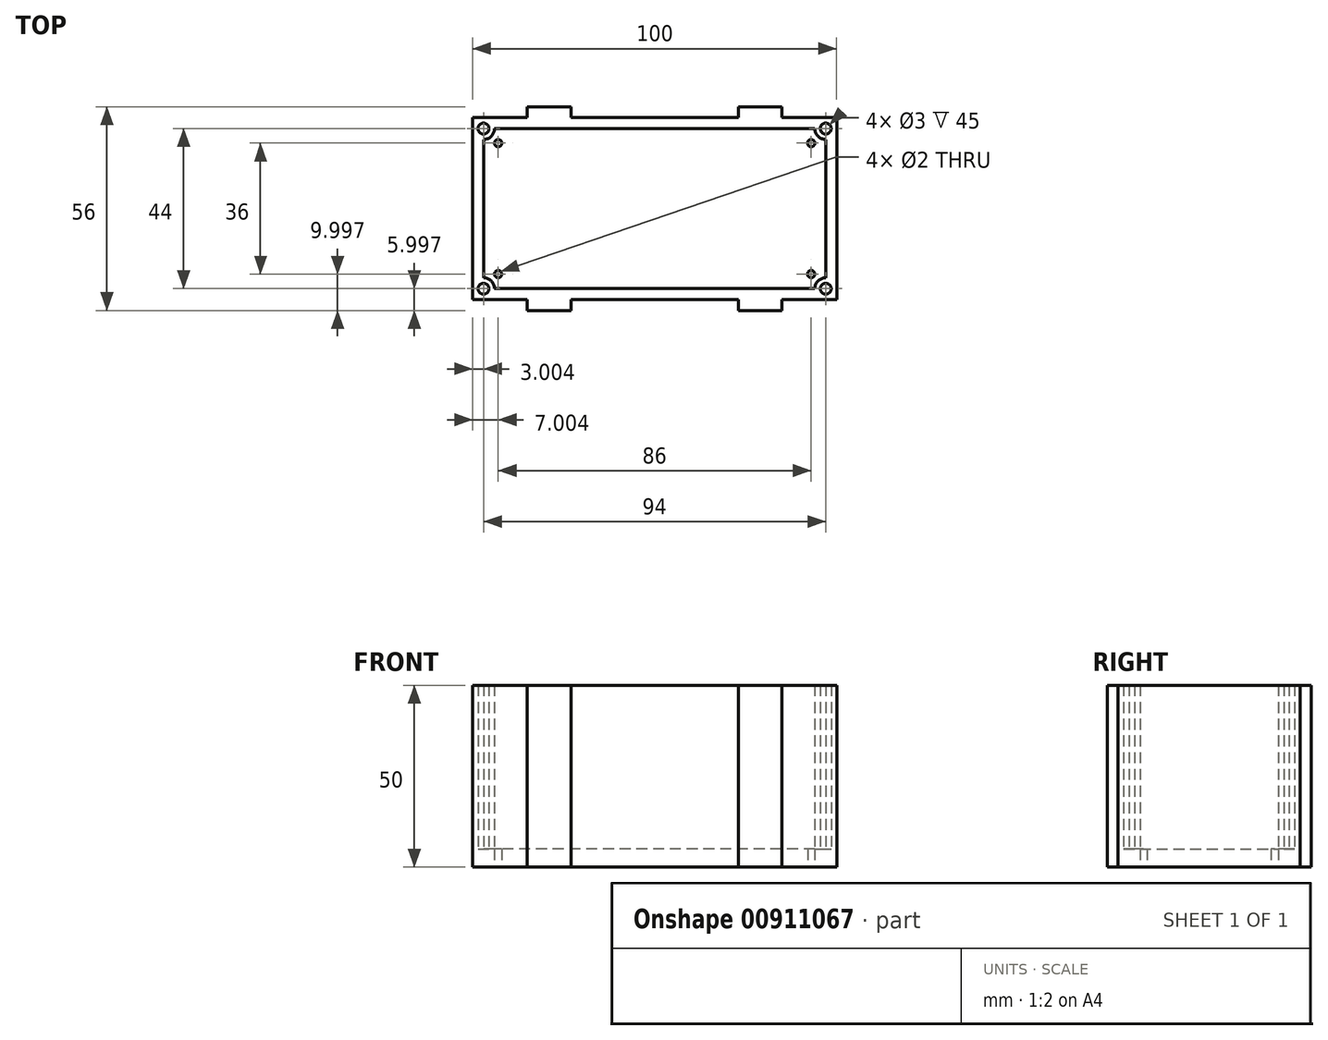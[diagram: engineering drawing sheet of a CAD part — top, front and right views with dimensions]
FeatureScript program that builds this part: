
annotation { "Feature Type Name" : "Feature", "Feature Type Description" : "" }
export const myFeature = defineFeature(function(context is Context, id is Id, definition is map)
    precondition{}
    {
        {
            var Q0;
            Q0=qCreatedBy(makeId("Top.planeOp"),FACE);
            var sketch = newSketch(context, id + "F0", { "sketchPlane" : qUnion([Q0])});
            skLineSegment(sketch, "E0.bottom", {"start": v(-49.27, 37.86) * mm, "end": v(50.73, 37.86) * mm});
            skLineSegment(sketch, "E0.top", {"start": v(-49.27, -12.14) * mm, "end": v(50.73, -12.14) * mm});
            skLineSegment(sketch, "E0.left", {"start": v(-49.27, 37.86) * mm, "end": v(-49.27, -12.14) * mm});
            skLineSegment(sketch, "E0.right", {"start": v(50.73, 37.86) * mm, "end": v(50.73, -12.14) * mm});
            skSolve(sketch);
        }
        {
            var Q0;
            Q0 = qSketchRegion(id + "F0", true);
            var Q1;
            Q1 = qSketchRegion(id + "F2", true);
            extrude(context, id + "F1", {"entities" : qUnion([Q0, Q1]), "depth" : 5 * mm, "offsetDistance" : 25 * mm});
        }
        {
            var Q0;
            Q0=makeQuery(id+"F1.opExtrude","CAP_FACE",FACE,{"disambiguationData":[OSD([sQuery(id+"F0.wireOp",EDGE,"E0.bottom"),sQuery(id+"F0.wireOp",EDGE,"E0.top"),sQuery(id+"F0.wireOp",EDGE,"E0.left"),sQuery(id+"F0.wireOp",EDGE,"E0.right")])],"isStart":false});
            var sketch = newSketch(context, id + "F2", { "sketchPlane" : qUnion([Q0])});
            skLineSegment(sketch, "E1.0", {"start": v(-46.27, 31.86) * mm, "end": v(-46.27, -6.14) * mm});
            skLineSegment(sketch, "E1.1", {"start": v(44.73, 34.86) * mm, "end": v(-43.27, 34.86) * mm});
            skLineSegment(sketch, "E1.2", {"start": v(47.73, -6.14) * mm, "end": v(47.73, 31.86) * mm});
            skLineSegment(sketch, "E1.3", {"start": v(-43.27, -9.14) * mm, "end": v(44.73, -9.14) * mm});
            skArc(sketch, "E2", {"start": v(-46.27, 31.86) * mm, "mid": v(-44.14, 32.74) * mm, "end": v(-43.27, 34.86) * mm});
            skArc(sketch, "E3", {"start": v(44.73, 34.86) * mm, "mid": v(45.61, 32.74) * mm, "end": v(47.73, 31.86) * mm});
            skArc(sketch, "E4", {"start": v(47.73, -6.14) * mm, "mid": v(45.61, -7.02) * mm, "end": v(44.73, -9.14) * mm});
            skArc(sketch, "E5", {"start": v(-43.27, -9.14) * mm, "mid": v(-44.14, -7.02) * mm, "end": v(-46.27, -6.14) * mm});
            skSolve(sketch);
        }
        {
            var Q0;
            Q0=makeQuery(id+"F2.imprint","IMPRINT",FACE,{"disambiguationData":[TD([[makeQuery(id+"F2.imprint","IMPRINT",EDGE,{"derivedFrom":sQuery(id+"F2.wireOp",EDGE,"E1.0")}),-1.0]])]});
            extrude(context, id + "F3", {"entities" : qUnion([Q0]), "operationType" : NewBodyOperationType.ADD, "depth" : 45 * mm, "offsetDistance" : 25 * mm});
        }
        {
            var Q0;
            {var subQ0=sQuery(id+"F0.wireOp",EDGE,"E0.top");Q0=makeQuery(id+"F3.boolean.opBoolean","MERGE",FACE,{"derivedFrom":[makeQuery(id+"F1.opExtrude","SWEPT_FACE",FACE,{"disambiguationData":[OSD([subQ0])]}),makeQuery(id+"F3.opExtrude","SWEPT_FACE",FACE,{"disambiguationData":[OSD([subQ0])]})]});}
            var sketch = newSketch(context, id + "F4", { "sketchPlane" : qUnion([Q0])});
            skLineSegment(sketch, "E6.bottom", {"start": v(-34.27, 0) * mm, "end": v(-22.27, 0) * mm});
            skLineSegment(sketch, "E6.top", {"start": v(-34.27, 50) * mm, "end": v(-22.27, 50) * mm});
            skLineSegment(sketch, "E6.left", {"start": v(-34.27, 0) * mm, "end": v(-34.27, 50) * mm});
            skLineSegment(sketch, "E6.right", {"start": v(-22.27, 0) * mm, "end": v(-22.27, 50) * mm});
            skLineSegment(sketch, "E7.bottom", {"start": v(23.73, 0) * mm, "end": v(35.73, 0) * mm});
            skLineSegment(sketch, "E7.top", {"start": v(23.73, 50) * mm, "end": v(35.73, 50) * mm});
            skLineSegment(sketch, "E7.left", {"start": v(23.73, 0) * mm, "end": v(23.73, 50) * mm});
            skLineSegment(sketch, "E7.right", {"start": v(35.73, 0) * mm, "end": v(35.73, 50) * mm});
            skSolve(sketch);
        }
        {
            var Q0;
            Q0=makeQuery(id+"F4.imprint","IMPRINT",FACE,{"disambiguationData":[TD([[makeQuery(id+"F4.imprint","IMPRINT",EDGE,{"derivedFrom":sQuery(id+"F4.wireOp",EDGE,"E6.bottom")}),1.0]])]});
            var Q1;
            Q1=makeQuery(id+"F4.imprint","IMPRINT",FACE,{"disambiguationData":[TD([[makeQuery(id+"F4.imprint","IMPRINT",EDGE,{"derivedFrom":sQuery(id+"F4.wireOp",EDGE,"E7.bottom")}),1.0]])]});
            extrude(context, id + "F5", {"entities" : qUnion([Q0, Q1]), "operationType" : NewBodyOperationType.ADD, "depth" : 3 * mm, "offsetDistance" : 25 * mm});
        }
        {
            var Q0;
            {var subQ0=sQuery(id+"F0.wireOp",EDGE,"E0.bottom");Q0=makeQuery(id+"F3.boolean.opBoolean","MERGE",FACE,{"derivedFrom":[makeQuery(id+"F1.opExtrude","SWEPT_FACE",FACE,{"disambiguationData":[OSD([subQ0])]}),makeQuery(id+"F3.opExtrude","SWEPT_FACE",FACE,{"disambiguationData":[OSD([subQ0])]})]});}
            var sketch = newSketch(context, id + "F6", { "sketchPlane" : qUnion([Q0])});
            skLineSegment(sketch, "E8.bottom", {"start": v(-35.73, 50) * mm, "end": v(-23.73, 50) * mm});
            skLineSegment(sketch, "E8.top", {"start": v(-35.73, 0) * mm, "end": v(-23.73, 0) * mm});
            skLineSegment(sketch, "E8.left", {"start": v(-35.73, 50) * mm, "end": v(-35.73, 0) * mm});
            skLineSegment(sketch, "E8.right", {"start": v(-23.73, 50) * mm, "end": v(-23.73, 0) * mm});
            skLineSegment(sketch, "E9.bottom", {"start": v(22.27, 50) * mm, "end": v(34.27, 50) * mm});
            skLineSegment(sketch, "E9.top", {"start": v(22.27, 0) * mm, "end": v(34.27, 0) * mm});
            skLineSegment(sketch, "E9.left", {"start": v(22.27, 50) * mm, "end": v(22.27, 0) * mm});
            skLineSegment(sketch, "E9.right", {"start": v(34.27, 50) * mm, "end": v(34.27, 0) * mm});
            skSolve(sketch);
        }
        {
            var Q0;
            Q0=makeQuery(id+"F6.imprint","IMPRINT",FACE,{"disambiguationData":[TD([[makeQuery(id+"F6.imprint","IMPRINT",EDGE,{"derivedFrom":sQuery(id+"F6.wireOp",EDGE,"E8.bottom")}),1.0]])]});
            var Q1;
            Q1=makeQuery(id+"F6.imprint","IMPRINT",FACE,{"disambiguationData":[TD([[makeQuery(id+"F6.imprint","IMPRINT",EDGE,{"derivedFrom":sQuery(id+"F6.wireOp",EDGE,"E9.bottom")}),1.0]])]});
            extrude(context, id + "F7", {"entities" : qUnion([Q0, Q1]), "operationType" : NewBodyOperationType.ADD, "depth" : 3 * mm, "offsetDistance" : 25 * mm});
        }
        {
            var Q0;
            Q0=sQuery(id+"F2.wireOp",VERTEX,"E2.center");
            var Q1;
            Q1=sQuery(id+"F2.wireOp",VERTEX,"E5.center");
            var Q2;
            Q2=sQuery(id+"F2.wireOp",VERTEX,"E3.center");
            var Q3;
            Q3=sQuery(id+"F2.wireOp",VERTEX,"E4.center");
            var Q4;
            Q4=makeQuery(id+"F1.opExtrude","SWEPT_BODY",BODY,{"disambiguationData":[OSD([sQuery(id+"F0.wireOp",EDGE,"E0.bottom"),sQuery(id+"F0.wireOp",EDGE,"E0.top"),sQuery(id+"F0.wireOp",EDGE,"E0.left"),sQuery(id+"F0.wireOp",EDGE,"E0.right")])]});
            hole(context, id + "F8", {"style" : HoleStyle.SIMPLE, "endStyle" : HoleEndStyle.BLIND, "oppositeDirection" : true, "holeDiameter" : 3 * mm, "majorDiameter" : 5 * mm, "holeDepth" : 45 * mm, "isTappedThrough" : true, "tappedDepth" : 12 * mm, "tapClearance" : 3, "locations" : qUnion([Q0, Q1, Q2, Q3]), "scope" : qUnion([Q4])});
        }
        {
            var Q0;
            Q0=makeQuery(id+"F7.boolean.opBoolean","MERGE",FACE,{"derivedFrom":[makeQuery(id+"F5.boolean.opBoolean","MERGE",FACE,{"derivedFrom":[makeQuery(id+"F1.opExtrude","CAP_FACE",FACE,{"disambiguationData":[OSD([sQuery(id+"F0.wireOp",EDGE,"E0.bottom"),sQuery(id+"F0.wireOp",EDGE,"E0.top"),sQuery(id+"F0.wireOp",EDGE,"E0.left"),sQuery(id+"F0.wireOp",EDGE,"E0.right")])],"isStart":true}),makeQuery(id+"F5.opExtrude","SWEPT_FACE",FACE,{"disambiguationData":[OSD([sQuery(id+"F4.wireOp",EDGE,"E6.bottom")])]}),makeQuery(id+"F5.opExtrude","SWEPT_FACE",FACE,{"disambiguationData":[OSD([sQuery(id+"F4.wireOp",EDGE,"E7.bottom")])]})]}),makeQuery(id+"F7.opExtrude","SWEPT_FACE",FACE,{"disambiguationData":[OSD([sQuery(id+"F6.wireOp",EDGE,"E8.top")])]}),makeQuery(id+"F7.opExtrude","SWEPT_FACE",FACE,{"disambiguationData":[OSD([sQuery(id+"F6.wireOp",EDGE,"E9.top")])]})]});
            var sketch = newSketch(context, id + "F9", { "sketchPlane" : qUnion([Q0])});
            skCircle(sketch, "E10", {"center": v(-42.27, 5.14) * mm, "radius": 2 * mm});
            skCircle(sketch, "E11", {"center": v(43.73, 5.14) * mm, "radius": 2 * mm});
            skCircle(sketch, "E12", {"center": v(-42.27, -30.86) * mm, "radius": 2 * mm});
            skCircle(sketch, "E13", {"center": v(43.73, -30.86) * mm, "radius": 2 * mm});
            skSolve(sketch);
        }
        {
            var Q0;
            Q0=sQuery(id+"F9.wireOp",EDGE,"E10");
            var Q1;
            Q1=sQuery(id+"F9.wireOp",EDGE,"E11");
            var Q2;
            Q2=sQuery(id+"F9.wireOp",EDGE,"E13");
            var Q3;
            Q3=sQuery(id+"F9.wireOp",EDGE,"E12");
            extrude(context, id + "F10", {"bodyType" : ToolBodyType.SURFACE, "surfaceEntities" : qUnion([Q0, Q1, Q2, Q3]), "oppositeDirection" : true, "depth" : 9 * mm, "offsetDistance" : 25 * mm});
        }
        {
            var Q0;
            Q0=sQuery(id+"F9.wireOp",VERTEX,"E10.center");
            var Q1;
            Q1=sQuery(id+"F9.wireOp",VERTEX,"E11.center");
            var Q2;
            Q2=sQuery(id+"F9.wireOp",VERTEX,"E13.center");
            var Q3;
            Q3=sQuery(id+"F9.wireOp",VERTEX,"E12.center");
            var Q4;
            Q4=makeQuery(id+"F1.opExtrude","SWEPT_BODY",BODY,{"disambiguationData":[OSD([sQuery(id+"F0.wireOp",EDGE,"E0.bottom"),sQuery(id+"F0.wireOp",EDGE,"E0.top"),sQuery(id+"F0.wireOp",EDGE,"E0.left"),sQuery(id+"F0.wireOp",EDGE,"E0.right")])]});
            hole(context, id + "F11", {"style" : HoleStyle.SIMPLE, "endStyle" : HoleEndStyle.BLIND, "holeDiameter" : 2 * mm, "majorDiameter" : 5 * mm, "holeDepth" : 20 * mm, "isTappedThrough" : true, "tappedDepth" : 12 * mm, "tapClearance" : 3, "locations" : qUnion([Q0, Q1, Q2, Q3]), "scope" : qUnion([Q4])});
        }
    });
